# Revit family: 304_01be67634ee84b2d9a1468c78c5465
name_source: partatom
category: Pipe Accessories
units: mm (PartAtom-declared; Revit-internal decimal feet)

## family parameters
Always vertical = Yes
Cut with Voids When Loaded = No
Part Type = Valve - Breaks Into
Round Connector Dimension = Use Diameter
Shared = No
Work Plane-Based = No

## types (10) — shared parameters
A = 30.00°
Description = Pressure independent control valve
H4 = 12 mm  [stored 0.0393701 ft]
H5 = 20 mm  [stored 0.0656168 ft]
L2D = 104 mm
L2D_Min = 3048 mm
Manufacturer = Frese A/S
PLG0 = Yes
QmdConnectorList = 301;D;302;D
R5 = 5 mm  [stored 0.0164042 ft]
R6 = 12 mm  [stored 0.0393701 ft]
R7 = 17 mm  [stored 0.0557743 ft]
R8 = 14 mm  [stored 0.0459318 ft]
R9 = 8 mm  [stored 0.0262467 ft]
URL = https://www.frese.eu
W2D = 32 mm  [stored 0.104987 ft]
magiPartTypeId = 304
magiProductFamilyId = 01be67634ee84b2d9a1468c78c5465

## per-type parameters (varying)
| type | CenSd_R1_6 | D | H1 | H2 | H3 | H6 | H6__ve | L1 | L1__ve | L2 | L3 | LL | R1 | R2 | R3 | R4 | X | Z | magiProductId |
| Frese OPTIMA Compact F/F 5.5 PT Plug DN32 | 23 mm | 32 mm | 46 mm  [stored 0.150919 ft] | 10 mm  [stored 0.0328084 ft] | 16 mm  [stored 0.0524934 ft] | 68 mm | -68 mm  [stored -0.223097 ft] | 19 mm  [stored 0.062336 ft] | -19 mm  [stored -0.062336 ft] | 67 mm | 13 mm  [stored 0.0426509 ft] | 52 mm  [stored 0.170604 ft] | 26 mm  [stored 0.0853018 ft] | 22 mm  [stored 0.0721785 ft] | 32 mm  [stored 0.104987 ft] | 29 mm  [stored 0.0951444 ft] | 13 mm  [stored 0.0426509 ft] | 1 mm  [stored 0.00328084 ft] | df1c00d195034ef0b1ec6dc57a3080 |
| Frese OPTIMA Compact F/F High 2.5 PT Plug DN15 | 13 mm  [stored 0.0426509 ft] | 15 mm | 26 mm  [stored 0.0853018 ft] | 8 mm  [stored 0.0262467 ft] | 18 mm  [stored 0.0590551 ft] | 57 mm  [stored 0.187008 ft] | -57 mm  [stored -0.187008 ft] | 14 mm  [stored 0.0459318 ft] | -14 mm | 48 mm  [stored 0.15748 ft] | 11 mm  [stored 0.0360892 ft] | 38 mm  [stored 0.124672 ft] | 15 mm  [stored 0.0492126 ft] | 12 mm  [stored 0.0393701 ft] | 19 mm  [stored 0.062336 ft] | 19 mm  [stored 0.062336 ft] | 7 mm  [stored 0.0229659 ft] | 0 mm  [stored 0 ft] | 89b348523dca4fefb6c7ae521abddd |
| Frese OPTIMA Compact F/F High 2.5 PT Plug DN20 | 15 mm  [stored 0.0492126 ft] | 20 mm | 26 mm  [stored 0.0853018 ft] | 8 mm  [stored 0.0262467 ft] | 18 mm  [stored 0.0590551 ft] | 60 mm | -60 mm | 14 mm  [stored 0.0459318 ft] | -14 mm | 51 mm | 11 mm  [stored 0.0360892 ft] | 40 mm | 18 mm  [stored 0.0590551 ft] | 14 mm  [stored 0.0459318 ft] | 19 mm  [stored 0.062336 ft] | 19 mm  [stored 0.062336 ft] | 10 mm  [stored 0.0328084 ft] | 0 mm  [stored 0 ft] | cf93e0f3640a42a8a678eca23d1527 |
| Frese OPTIMA Compact F/F High 5.0 PT Plug DN15 | 13 mm  [stored 0.0426509 ft] | 15 mm | 26 mm  [stored 0.0853018 ft] | 8 mm  [stored 0.0262467 ft] | 18 mm  [stored 0.0590551 ft] | 57 mm  [stored 0.187008 ft] | -57 mm  [stored -0.187008 ft] | 14 mm  [stored 0.0459318 ft] | -14 mm | 48 mm  [stored 0.15748 ft] | 11 mm  [stored 0.0360892 ft] | 38 mm  [stored 0.124672 ft] | 15 mm  [stored 0.0492126 ft] | 12 mm  [stored 0.0393701 ft] | 19 mm  [stored 0.062336 ft] | 19 mm  [stored 0.062336 ft] | 7 mm  [stored 0.0229659 ft] | 0 mm  [stored 0 ft] | 2e6505697e744e01b0ad9c2d669662 |
| Frese OPTIMA Compact F/F High 5.0 PT Plug DN20 | 15 mm  [stored 0.0492126 ft] | 20 mm | 26 mm  [stored 0.0853018 ft] | 8 mm  [stored 0.0262467 ft] | 18 mm  [stored 0.0590551 ft] | 60 mm | -60 mm | 14 mm  [stored 0.0459318 ft] | -14 mm | 51 mm | 11 mm  [stored 0.0360892 ft] | 40 mm | 18 mm  [stored 0.0590551 ft] | 14 mm  [stored 0.0459318 ft] | 19 mm  [stored 0.062336 ft] | 19 mm  [stored 0.062336 ft] | 10 mm  [stored 0.0328084 ft] | 0 mm  [stored 0 ft] | 3b063aaad6f44e8dbcb4679e4a622e |
| Frese OPTIMA Compact F/F High 5.5 PT Plug DN20 | 15 mm  [stored 0.0492126 ft] | 20 mm | 26 mm  [stored 0.0853018 ft] | 8 mm  [stored 0.0262467 ft] | 18 mm  [stored 0.0590551 ft] | 60 mm | -60 mm | 14 mm  [stored 0.0459318 ft] | -14 mm | 51 mm | 11 mm  [stored 0.0360892 ft] | 40 mm | 18 mm  [stored 0.0590551 ft] | 14 mm  [stored 0.0459318 ft] | 19 mm  [stored 0.062336 ft] | 19 mm  [stored 0.062336 ft] | 10 mm  [stored 0.0328084 ft] | 0 mm  [stored 0 ft] | 6f2e419bcadf4dd2a9ff6e694a03fa |
| Frese OPTIMA Compact F/F High 5.5 PT Plug DN25L | 19 mm  [stored 0.062336 ft] | 25 mm | 43 mm  [stored 0.141076 ft] | 10 mm  [stored 0.0328084 ft] | 16 mm  [stored 0.0524934 ft] | 64 mm | -64 mm  [stored -0.209974 ft] | 18 mm  [stored 0.0590551 ft] | -18 mm  [stored -0.0590551 ft] | 64 mm | 13 mm  [stored 0.0426509 ft] | 50 mm  [stored 0.164042 ft] | 22 mm  [stored 0.0721785 ft] | 19 mm  [stored 0.062336 ft] | 32 mm  [stored 0.104987 ft] | 29 mm  [stored 0.0951444 ft] | 13 mm  [stored 0.0426509 ft] | 0 mm  [stored 0 ft] | d9f644dbdce8417aa9c852cd9f0b5f |
| Frese OPTIMA Compact F/F Low 2.5 PT Plug DN15 | 13 mm  [stored 0.0426509 ft] | 15 mm | 26 mm  [stored 0.0853018 ft] | 8 mm  [stored 0.0262467 ft] | 18 mm  [stored 0.0590551 ft] | 57 mm  [stored 0.187008 ft] | -57 mm  [stored -0.187008 ft] | 14 mm  [stored 0.0459318 ft] | -14 mm | 48 mm  [stored 0.15748 ft] | 11 mm  [stored 0.0360892 ft] | 38 mm  [stored 0.124672 ft] | 15 mm  [stored 0.0492126 ft] | 12 mm  [stored 0.0393701 ft] | 19 mm  [stored 0.062336 ft] | 19 mm  [stored 0.062336 ft] | 7 mm  [stored 0.0229659 ft] | 0 mm  [stored 0 ft] | cb9bcb51ec7642e1b2f50ebebd6939 |
| Frese OPTIMA Compact F/F Low 5.0 PT Plug DN15 | 13 mm  [stored 0.0426509 ft] | 15 mm | 26 mm  [stored 0.0853018 ft] | 8 mm  [stored 0.0262467 ft] | 18 mm  [stored 0.0590551 ft] | 57 mm  [stored 0.187008 ft] | -57 mm  [stored -0.187008 ft] | 14 mm  [stored 0.0459318 ft] | -14 mm | 48 mm  [stored 0.15748 ft] | 11 mm  [stored 0.0360892 ft] | 38 mm  [stored 0.124672 ft] | 15 mm  [stored 0.0492126 ft] | 12 mm  [stored 0.0393701 ft] | 19 mm  [stored 0.062336 ft] | 19 mm  [stored 0.062336 ft] | 7 mm  [stored 0.0229659 ft] | 0 mm  [stored 0 ft] | cc72561b73f74a7f910c49d1f48a4b |
| Frese OPTIMA Compact F/F Low 5.5 PT Plug DN25 | 19 mm  [stored 0.062336 ft] | 25 mm | 43 mm  [stored 0.141076 ft] | 10 mm  [stored 0.0328084 ft] | 16 mm  [stored 0.0524934 ft] | 64 mm | -64 mm  [stored -0.209974 ft] | 15 mm  [stored 0.0492126 ft] | -15 mm | 53 mm | 13 mm  [stored 0.0426509 ft] | 42 mm | 22 mm  [stored 0.0721785 ft] | 19 mm  [stored 0.062336 ft] | 19 mm  [stored 0.062336 ft] | 19 mm  [stored 0.062336 ft] | 13 mm  [stored 0.0426509 ft] | 0 mm  [stored 0 ft] | 5ad9d9783e2c493baec58790ac6c15 |

note: column(s) folded — value = type name in every type: MC Product Code

note: [stored X ft] marks values corroborated as IEEE doubles in the binary element streams (Revit-internal decimal feet)

## geometry (parser evidence)
native form markers: Sweep x1
no freeform markers — native parametric forms only
